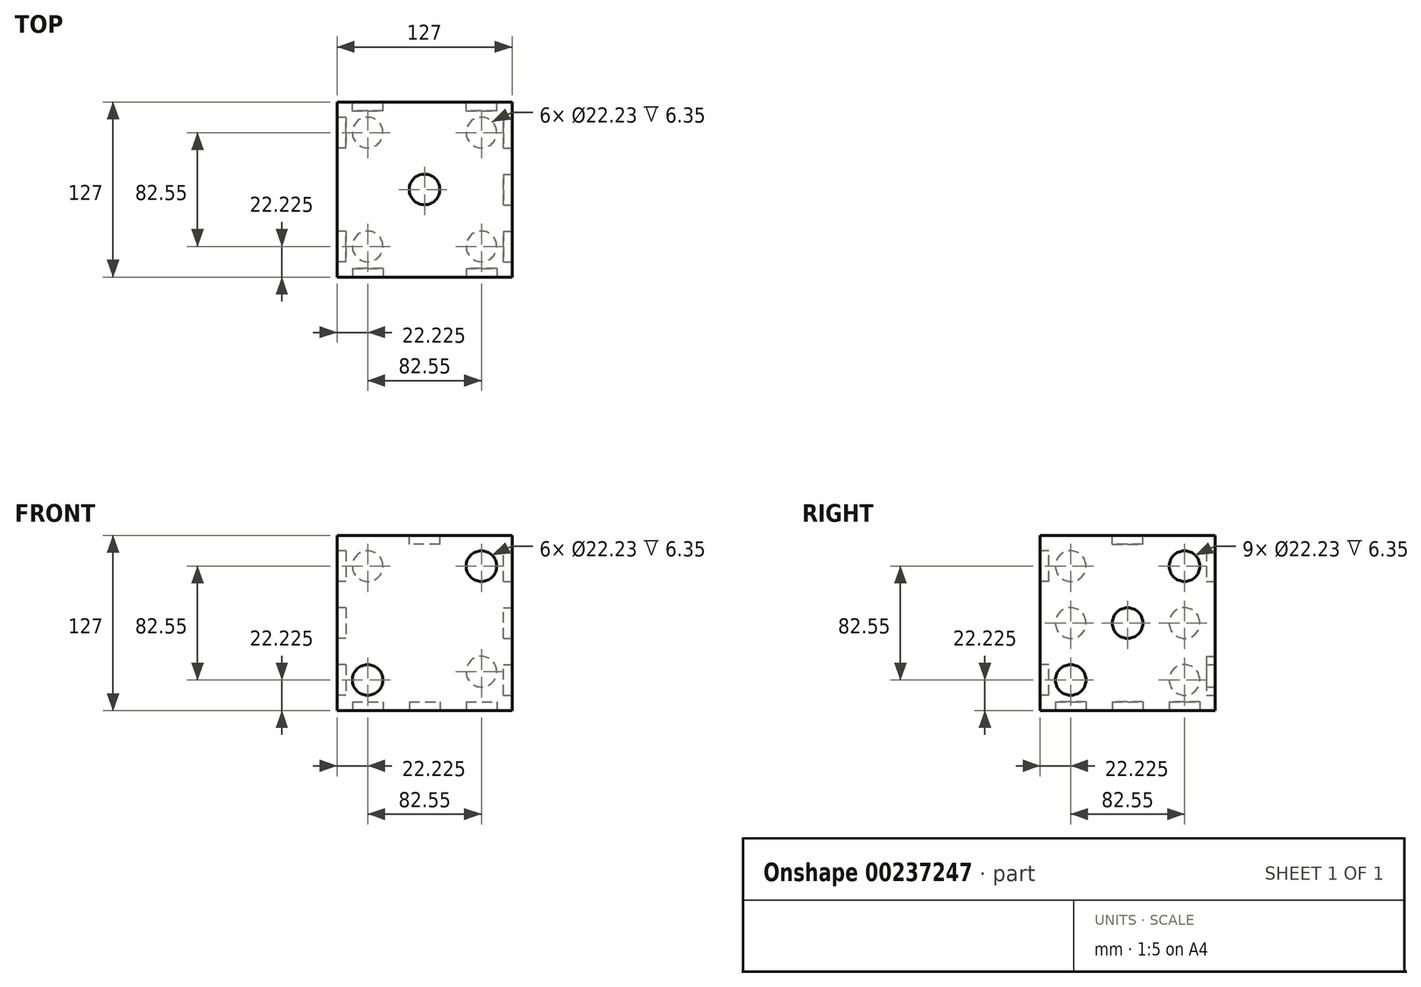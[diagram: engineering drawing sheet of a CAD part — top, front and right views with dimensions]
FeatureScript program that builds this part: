
annotation { "Feature Type Name" : "Feature", "Feature Type Description" : "" }
export const myFeature = defineFeature(function(context is Context, id is Id, definition is map)
    precondition{}
    {
        {
            var Q0;
            Q0=qCreatedBy(makeId("Top.planeOp"),FACE);
            var sketch = newSketch(context, id + "F0", { "sketchPlane" : qUnion([Q0])});
            skLineSegment(sketch, "E0.bottom", {"start": v(0, 0) * mm, "end": v(127, 0) * mm});
            skLineSegment(sketch, "E0.top", {"start": v(0, 127) * mm, "end": v(127, 127) * mm});
            skLineSegment(sketch, "E0.left", {"start": v(0, 0) * mm, "end": v(0, 127) * mm});
            skLineSegment(sketch, "E0.right", {"start": v(127, 0) * mm, "end": v(127, 127) * mm});
            skSolve(sketch);
        }
        {
            var Q0;
            Q0=makeQuery(id+"F0.imprint","IMPRINT",FACE,{"disambiguationData":[TD([[makeQuery(id+"F0.imprint","IMPRINT",EDGE,{"derivedFrom":sQuery(id+"F0.wireOp",EDGE,"E0.bottom")}),1.0]])]});
            extrude(context, id + "F1", {"entities" : qUnion([Q0]), "depth" : 127 * mm});
        }
        {
            var Q0;
            Q0=makeQuery(id+"F1.opExtrude","CAP_FACE",FACE,{"disambiguationData":[OSD([sQuery(id+"F0.wireOp",EDGE,"E0.bottom"),sQuery(id+"F0.wireOp",EDGE,"E0.top"),sQuery(id+"F0.wireOp",EDGE,"E0.left"),sQuery(id+"F0.wireOp",EDGE,"E0.right")])],"isStart":false});
            var sketch = newSketch(context, id + "F2", { "sketchPlane" : qUnion([Q0])});
            skCircle(sketch, "E1", {"center": v(63.5, 63.5) * mm, "radius": 11.11 * mm});
            skSolve(sketch);
        }
        {
            var Q0;
            Q0=makeQuery(id+"F2.imprint","IMPRINT",FACE,{"disambiguationData":[TD([[makeQuery(id+"F2.imprint","IMPRINT",EDGE,{"derivedFrom":sQuery(id+"F2.wireOp",EDGE,"E1")}),1.0]])]});
            extrude(context, id + "F3", {"entities" : qUnion([Q0]), "operationType" : NewBodyOperationType.REMOVE, "oppositeDirection" : true, "depth" : 6.35 * mm});
        }
        {
            var Q0;
            Q0=makeQuery(id+"F1.opExtrude","SWEPT_FACE",FACE,{"disambiguationData":[OSD([sQuery(id+"F0.wireOp",EDGE,"E0.bottom")])]});
            var sketch = newSketch(context, id + "F4", { "sketchPlane" : qUnion([Q0])});
            skCircle(sketch, "E2", {"center": v(22.22, 22.22) * mm, "radius": 11.11 * mm});
            skCircle(sketch, "E3", {"center": v(104.78, 104.78) * mm, "radius": 11.11 * mm});
            skSolve(sketch);
        }
        {
            var Q0;
            Q0 = qSketchRegion(id + "F4", true);
            extrude(context, id + "F5", {"entities" : qUnion([Q0]), "operationType" : NewBodyOperationType.REMOVE, "oppositeDirection" : true, "depth" : 6.35 * mm});
        }
        {
            var Q0;
            Q0=makeQuery(id+"F1.opExtrude","SWEPT_FACE",FACE,{"disambiguationData":[OSD([sQuery(id+"F0.wireOp",EDGE,"E0.right")])]});
            var sketch = newSketch(context, id + "F6", { "sketchPlane" : qUnion([Q0])});
            skLineSegment(sketch, "E4", {"start": v(0, 0) * mm, "end": v(127, 127) * mm, "construction": true});
            skCircle(sketch, "E5", {"center": v(22.22, 22.23) * mm, "radius": 11.11 * mm});
            skCircle(sketch, "E6", {"center": v(63.5, 63.5) * mm, "radius": 11.11 * mm});
            skCircle(sketch, "E7", {"center": v(104.77, 104.78) * mm, "radius": 11.11 * mm});
            skSolve(sketch);
        }
        {
            var Q0;
            Q0 = qSketchRegion(id + "F6", true);
            extrude(context, id + "F7", {"entities" : qUnion([Q0]), "operationType" : NewBodyOperationType.REMOVE, "oppositeDirection" : true, "depth" : 6.35 * mm});
        }
        {
            var Q0;
            Q0=makeQuery(id+"F1.opExtrude","SWEPT_FACE",FACE,{"disambiguationData":[OSD([sQuery(id+"F0.wireOp",EDGE,"E0.top")])]});
            var sketch = newSketch(context, id + "F8", { "sketchPlane" : qUnion([Q0])});
            skCircle(sketch, "E8", {"center": v(-22.23, 104.78) * mm, "radius": 11.11 * mm});
            skCircle(sketch, "E9", {"center": v(-104.77, 104.78) * mm, "radius": 11.11 * mm});
            skCircle(sketch, "E10", {"center": v(-104.77, 28.23) * mm, "radius": 11.11 * mm});
            skCircle(sketch, "E11", {"center": v(-22.23, 22.22) * mm, "radius": 11.11 * mm});
            skSolve(sketch);
        }
        {
            var Q0;
            Q0 = qSketchRegion(id + "F8", true);
            extrude(context, id + "F9", {"entities" : qUnion([Q0]), "operationType" : NewBodyOperationType.REMOVE, "oppositeDirection" : true, "depth" : 6.35 * mm});
        }
        {
            var Q0;
            Q0=makeQuery(id+"F1.opExtrude","CAP_FACE",FACE,{"disambiguationData":[OSD([sQuery(id+"F0.wireOp",EDGE,"E0.bottom"),sQuery(id+"F0.wireOp",EDGE,"E0.top"),sQuery(id+"F0.wireOp",EDGE,"E0.left"),sQuery(id+"F0.wireOp",EDGE,"E0.right")])],"isStart":true});
            var sketch = newSketch(context, id + "F10", { "sketchPlane" : qUnion([Q0])});
            skLineSegment(sketch, "E12", {"start": v(0, -127) * mm, "end": v(127, 0) * mm, "construction": true});
            skCircle(sketch, "E13", {"center": v(22.22, -104.78) * mm, "radius": 11.11 * mm});
            skCircle(sketch, "E14", {"center": v(63.5, -63.5) * mm, "radius": 11.11 * mm});
            skCircle(sketch, "E15", {"center": v(104.78, -22.22) * mm, "radius": 11.11 * mm});
            skCircle(sketch, "E16", {"center": v(22.23, -22.23) * mm, "radius": 11.11 * mm});
            skCircle(sketch, "E17", {"center": v(104.77, -104.78) * mm, "radius": 11.11 * mm});
            skSolve(sketch);
        }
        {
            var Q0;
            Q0 = qSketchRegion(id + "F10", true);
            extrude(context, id + "F11", {"entities" : qUnion([Q0]), "operationType" : NewBodyOperationType.REMOVE, "oppositeDirection" : true, "depth" : 6.35 * mm});
        }
        {
            var Q0;
            Q0=makeQuery(id+"F1.opExtrude","SWEPT_FACE",FACE,{"disambiguationData":[OSD([sQuery(id+"F0.wireOp",EDGE,"E0.left")])]});
            var sketch = newSketch(context, id + "F12", { "sketchPlane" : qUnion([Q0])});
            skLineSegment(sketch, "E18", {"start": v(-104.78, 127) * mm, "end": v(-104.78, 0) * mm, "construction": true});
            skLineSegment(sketch, "E19", {"start": v(-22.23, 127) * mm, "end": v(-22.22, 0) * mm, "construction": true});
            skCircle(sketch, "E20", {"center": v(-104.78, 104.78) * mm, "radius": 11.11 * mm});
            skCircle(sketch, "E21", {"center": v(-104.78, 63.5) * mm, "radius": 11.11 * mm});
            skCircle(sketch, "E22", {"center": v(-104.78, 22.23) * mm, "radius": 11.11 * mm});
            skCircle(sketch, "E23", {"center": v(-22.23, 104.78) * mm, "radius": 11.11 * mm});
            skCircle(sketch, "E24", {"center": v(-22.23, 63.5) * mm, "radius": 11.11 * mm});
            skCircle(sketch, "E25", {"center": v(-22.22, 22.23) * mm, "radius": 11.11 * mm});
            skSolve(sketch);
        }
        {
            var Q0;
            Q0 = qSketchRegion(id + "F12", true);
            extrude(context, id + "F13", {"entities" : qUnion([Q0]), "operationType" : NewBodyOperationType.REMOVE, "oppositeDirection" : true, "depth" : 6.35 * mm});
        }
    });
